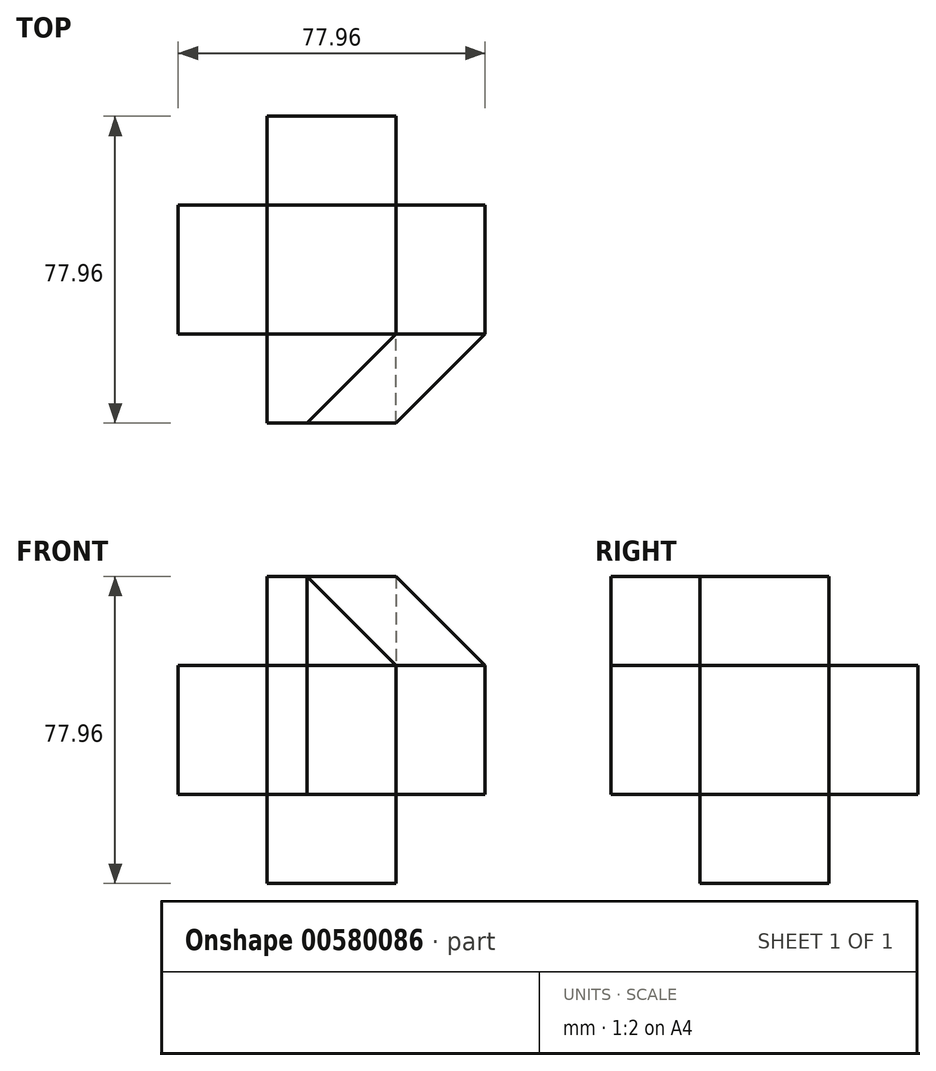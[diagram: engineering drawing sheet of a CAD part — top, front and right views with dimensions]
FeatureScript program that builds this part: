
annotation { "Feature Type Name" : "Feature", "Feature Type Description" : "" }
export const myFeature = defineFeature(function(context is Context, id is Id, definition is map)
    precondition{}
    {
        {
            var Q0;
            Q0=qCreatedBy(makeId("Front.planeOp"),FACE);
            var sketch = newSketch(context, id + "F0", { "sketchPlane" : qUnion([Q0])});
            skLineSegment(sketch, "E0.bottom", {"start": v(-16.36, 16.36) * mm, "end": v(16.36, 16.36) * mm});
            skLineSegment(sketch, "E0.top", {"start": v(-16.36, -16.36) * mm, "end": v(16.36, -16.36) * mm});
            skLineSegment(sketch, "E0.left", {"start": v(-16.36, 16.36) * mm, "end": v(-16.36, -16.36) * mm});
            skLineSegment(sketch, "E0.right", {"start": v(16.36, 16.36) * mm, "end": v(16.36, -16.36) * mm});
            skPoint(sketch, "E0.middle", {"position": v(0, 0) * mm});
            skSolve(sketch);
        }
        {
            var Q0;
            Q0=makeQuery(id+"F0.imprint","IMPRINT",FACE,{"disambiguationData":[TD([[makeQuery(id+"F0.imprint","IMPRINT",EDGE,{"derivedFrom":sQuery(id+"F0.wireOp",EDGE,"E0.bottom")}),-1.0]])]});
            extrude(context, id + "F1", {"entities" : qUnion([Q0]), "endBound" : BoundingType.SYMMETRIC, "depth" : 32.7 * mm, "offsetDistance" : 25 * mm});
        }
        {
            var Q0;
            Q0=makeQuery(id+"F1.opExtrude","SWEPT_FACE",FACE,{"disambiguationData":[OSD([sQuery(id+"F0.wireOp",EDGE,"E0.left")])]});
            extrude(context, id + "F2", {"entities" : qUnion([Q0]), "depth" : 22.63 * mm, "offsetDistance" : 25 * mm});
        }
        {
            var Q0;
            Q0=makeQuery(id+"F1.opExtrude","CAP_FACE",FACE,{"disambiguationData":[OSD([sQuery(id+"F0.wireOp",EDGE,"E0.bottom"),sQuery(id+"F0.wireOp",EDGE,"E0.top"),sQuery(id+"F0.wireOp",EDGE,"E0.left"),sQuery(id+"F0.wireOp",EDGE,"E0.right")])],"isStart":false});
            extrude(context, id + "F3", {"entities" : qUnion([Q0]), "depth" : 22.63 * mm, "offsetDistance" : 25 * mm});
        }
        {
            var Q0;
            Q0=makeQuery(id+"F1.opExtrude","SWEPT_FACE",FACE,{"disambiguationData":[OSD([sQuery(id+"F0.wireOp",EDGE,"E0.right")])]});
            extrude(context, id + "F4", {"entities" : qUnion([Q0]), "depth" : 22.63 * mm, "offsetDistance" : 25 * mm});
        }
        {
            var Q0;
            Q0=makeQuery(id+"F1.opExtrude","CAP_FACE",FACE,{"disambiguationData":[OSD([sQuery(id+"F0.wireOp",EDGE,"E0.bottom"),sQuery(id+"F0.wireOp",EDGE,"E0.top"),sQuery(id+"F0.wireOp",EDGE,"E0.left"),sQuery(id+"F0.wireOp",EDGE,"E0.right")])],"isStart":true});
            extrude(context, id + "F5", {"entities" : qUnion([Q0]), "depth" : 22.63 * mm, "offsetDistance" : 25 * mm});
        }
        {
            var Q0;
            Q0=makeQuery(id+"F1.opExtrude","SWEPT_FACE",FACE,{"disambiguationData":[OSD([sQuery(id+"F0.wireOp",EDGE,"E0.bottom")])]});
            extrude(context, id + "F6", {"entities" : qUnion([Q0]), "depth" : 22.63 * mm, "offsetDistance" : 25 * mm});
        }
        {
            var Q0;
            Q0=makeQuery(id+"F1.opExtrude","SWEPT_FACE",FACE,{"disambiguationData":[OSD([sQuery(id+"F0.wireOp",EDGE,"E0.top")])]});
            extrude(context, id + "F7", {"entities" : qUnion([Q0]), "operationType" : NewBodyOperationType.ADD, "depth" : 22.63 * mm, "offsetDistance" : 25 * mm});
        }
        {
            var Q0;
            Q0=makeQuery(id+"F3.opExtrude","SWEPT_BODY",BODY,{"disambiguationData":[OSD([sQuery(id+"F0.wireOp",EDGE,"E0.bottom"),sQuery(id+"F0.wireOp",EDGE,"E0.top"),sQuery(id+"F0.wireOp",EDGE,"E0.left"),sQuery(id+"F0.wireOp",EDGE,"E0.right")])]});
            var Q1;
            Q1=makeQuery(id+"F4.opExtrude","SWEPT_BODY",BODY,{"disambiguationData":[OSD([sQuery(id+"F0.wireOp",EDGE,"E0.right")])]});
            var Q2;
            Q2=makeQuery(id+"F5.opExtrude","SWEPT_BODY",BODY,{"disambiguationData":[OSD([sQuery(id+"F0.wireOp",EDGE,"E0.bottom"),sQuery(id+"F0.wireOp",EDGE,"E0.top"),sQuery(id+"F0.wireOp",EDGE,"E0.left"),sQuery(id+"F0.wireOp",EDGE,"E0.right")])]});
            var Q3;
            Q3=makeQuery(id+"F6.opExtrude","SWEPT_BODY",BODY,{"disambiguationData":[OSD([sQuery(id+"F0.wireOp",EDGE,"E0.bottom")])]});
            var Q4;
            Q4=makeQuery(id+"F1.opExtrude","SWEPT_BODY",BODY,{"disambiguationData":[OSD([sQuery(id+"F0.wireOp",EDGE,"E0.bottom"),sQuery(id+"F0.wireOp",EDGE,"E0.top"),sQuery(id+"F0.wireOp",EDGE,"E0.left"),sQuery(id+"F0.wireOp",EDGE,"E0.right")])]});
            var Q5;
            Q5=makeQuery(id+"F2.opExtrude","SWEPT_BODY",BODY,{"disambiguationData":[OSD([sQuery(id+"F0.wireOp",EDGE,"E0.left")])]});
            booleanBodies(context, id + "F8", {"operationType" : BooleanOperationType.UNION, "tools" : qUnion([Q0, Q1, Q2, Q3, Q4, Q5])});
        }
        {
            var Q0;
            {var subQ0=sQuery(id+"F0.wireOp",EDGE,"E0.top");var subQ1=sQuery(id+"F0.wireOp",EDGE,"E0.right");var subQ2=sQuery(id+"F0.wireOp",EDGE,"E0.left");var subQ3=sQuery(id+"F0.wireOp",EDGE,"E0.bottom");Q0=makeQuery(id+"F8.opBoolean","MERGE",FACE,{"disambiguationData":[OD(2.0)],"derivedFrom":[makeQuery(id+"F2.opExtrude","SWEPT_FACE",FACE,{"disambiguationData":[OSD([subQ2]),TDD([makeQuery(id+"F1.opExtrude","CAP_EDGE",EDGE,{"disambiguationData":[OSD([subQ2])],"isStart":false})])]}),makeQuery(id+"F4.opExtrude","SWEPT_FACE",FACE,{"disambiguationData":[OSD([subQ1]),TDD([makeQuery(id+"F1.opExtrude","CAP_EDGE",EDGE,{"disambiguationData":[OSD([subQ1])],"isStart":false})])]}),makeQuery(id+"F6.opExtrude","SWEPT_FACE",FACE,{"disambiguationData":[OSD([subQ3]),TDD([makeQuery(id+"F1.opExtrude","CAP_EDGE",EDGE,{"disambiguationData":[OSD([subQ3])],"isStart":false})])]}),makeQuery(id+"F7.boolean.opBoolean","MERGE",FACE,{"derivedFrom":[makeQuery(id+"F1.opExtrude","CAP_FACE",FACE,{"disambiguationData":[OSD([subQ3,subQ0,subQ2,subQ1])],"isStart":false}),makeQuery(id+"F7.opExtrude","SWEPT_FACE",FACE,{"disambiguationData":[OSD([subQ0]),TDD([makeQuery(id+"F1.opExtrude","CAP_EDGE",EDGE,{"disambiguationData":[OSD([subQ0])],"isStart":false})])]})]})]});}
            var sketch = newSketch(context, id + "F9", { "sketchPlane" : qUnion([Q0])});
            skLineSegment(sketch, "E1", {"start": v(16.36, 16.36) * mm, "end": v(38.98, 16.36) * mm});
            skLineSegment(sketch, "E2", {"start": v(38.98, 16.36) * mm, "end": v(16.36, 38.98) * mm});
            skLineSegment(sketch, "E3", {"start": v(16.36, 38.98) * mm, "end": v(16.36, 16.36) * mm});
            skSolve(sketch);
        }
        {
            var Q0;
            Q0=makeQuery(id+"F3.opExtrude","SWEPT_FACE",FACE,{"disambiguationData":[OSD([sQuery(id+"F0.wireOp",EDGE,"E0.bottom")])]});
            var sketch = newSketch(context, id + "F10", { "sketchPlane" : qUnion([Q0])});
            skLineSegment(sketch, "E4", {"start": v(16.36, -38.98) * mm, "end": v(16.36, -16.36) * mm});
            skLineSegment(sketch, "E5", {"start": v(16.36, -16.36) * mm, "end": v(38.98, -16.36) * mm});
            skLineSegment(sketch, "E6", {"start": v(38.98, -16.36) * mm, "end": v(16.36, -38.98) * mm});
            skSolve(sketch);
        }
        {
            var Q0;
            Q0=makeQuery(id+"F9.imprint","IMPRINT",FACE,{"disambiguationData":[TD([[makeQuery(id+"F9.imprint","IMPRINT",EDGE,{"derivedFrom":sQuery(id+"F9.wireOp",EDGE,"E1")}),1.0]])]});
            var Q1;
            Q1=sQuery(id+"F10.wireOp",EDGE,"E6");
            sweep(context, id + "F11", {"profiles" : qUnion([Q0]), "path" : qUnion([Q1])});
        }
    });
